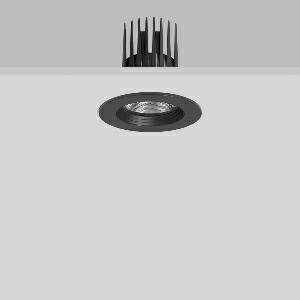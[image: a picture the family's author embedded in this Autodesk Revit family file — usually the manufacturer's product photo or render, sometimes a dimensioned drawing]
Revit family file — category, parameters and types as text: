
# Revit family: heledon_mini_e_901749_003_2_76_c3d3
name_source: partatom
category: Lighting Fixtures
units: mm (PartAtom-declared; Revit-internal decimal feet)

## family parameters
Cut with Voids When Loaded = No
Host = Face
Light Source = No
Part Type = Normal
Room Calculation Point = No
Round Connector Dimension = Use Diameter
Shared = No

## types (1)
- HELEDON mini E (1 x LED Modul 927, 3300 lm, 2700)
    Apparent Load = 29 VA
    Approval mark = CE
    CIE Flux Codes = 99 100 100 100 100
    Color Rendering = 92
    Color Temperature = 2700
    Default Elevation = 1800 mm
    Description = Series: HELEDON mini
Round recessed downlight. Housing: die-cast aluminium, powder-coated. Black plastic ring and recessed LED to prevent glare from the side. Optical assembly with reflector made of MIRO-Silver with 98% total light reflection for outstanding efficiency - can be changed without tools. Best colour rendering index Ra>90. Suitable for Recessed ceiling mounting. Installation without tools thanks to spring fastening system. Including separate LED converter with connecting cable 600 mm.High quality converter without flickering and stroboscopic effect. Through-wiring box (5 pole) available as accessory. The following accessories can be mounted without use of tools: interchangeable lenses, decorative glasses, honeycomb louvre, clear and frosted diffusers, white interchangeable plastic ring. 
Colour: deep black, matt (RAL 9005)
Diameter: 124 mm
Height: 3 mm
Cut-out diameter: 114 mm
Recess height: 170 mm
Luminaire: recess height: 120 mm
Lamp: LED
Socket: without socket
Colour temperature: 2700K
Colour rendering index (CRI): 92
System power: 29 W
Rated luminous flux: 3300 lm
Luminous efficiency: 114 lm/W
Control gear: Converter, dimmable, DALI
Protection class: II
Type of protection: IP 20
    Height = 0 mm  [stored 0 ft]
    Lamp = 1 x LED Modul 927
    Lamp Light Flux = 3300 lm
    Lamp count = 1
    Length = 124 mm  [stored 0.406824 ft]
    Lifetime = 50000 h
    Luminous efficacy = 114 lm/W
    Manufacturer = RZB
    ModVariant = No
    Model = 901749.003.2.76
    Mounting Place = Ceiling
    Mounting Type = Recessed
    Number of Poles = 1
    OnlyDefault = Yes
    Power Factor = 1
    Product Name = HELEDON mini E
    Product group = Recessed downlights
    ProductGroupID = 402
    Protection Class = Protection class II
    Protection Degree = IP 20
    RLX_Detail_Level = 1
    RLX_Emergency_Light_Flux = 0 lm
    RLX_Emergency_Type = 0
    RLX_Emergency_Type_DB = No
    RlxData = <blob elided: 124081 chars, md5=6fb77692>
    Socket = socket
    Standby Power = 0 W
    System Light Flux = 3300 lm
    System Power = 29 W
    Type Comments = Product without accessories
    Type Image = 901657.003.jpg
    URL = http://relux.com
    VarID = ---
    Voltage = 230 V
    Voltage Range = 220-240 V
    Weight = 0.00 kg
    Width = 0 mm  [stored 0 ft]

note: [stored X ft] marks values corroborated as IEEE doubles in the binary element streams (Revit-internal decimal feet)

## geometry (parser evidence)
native form markers: Blend x4, Sweep x11
no freeform markers — native parametric forms only
